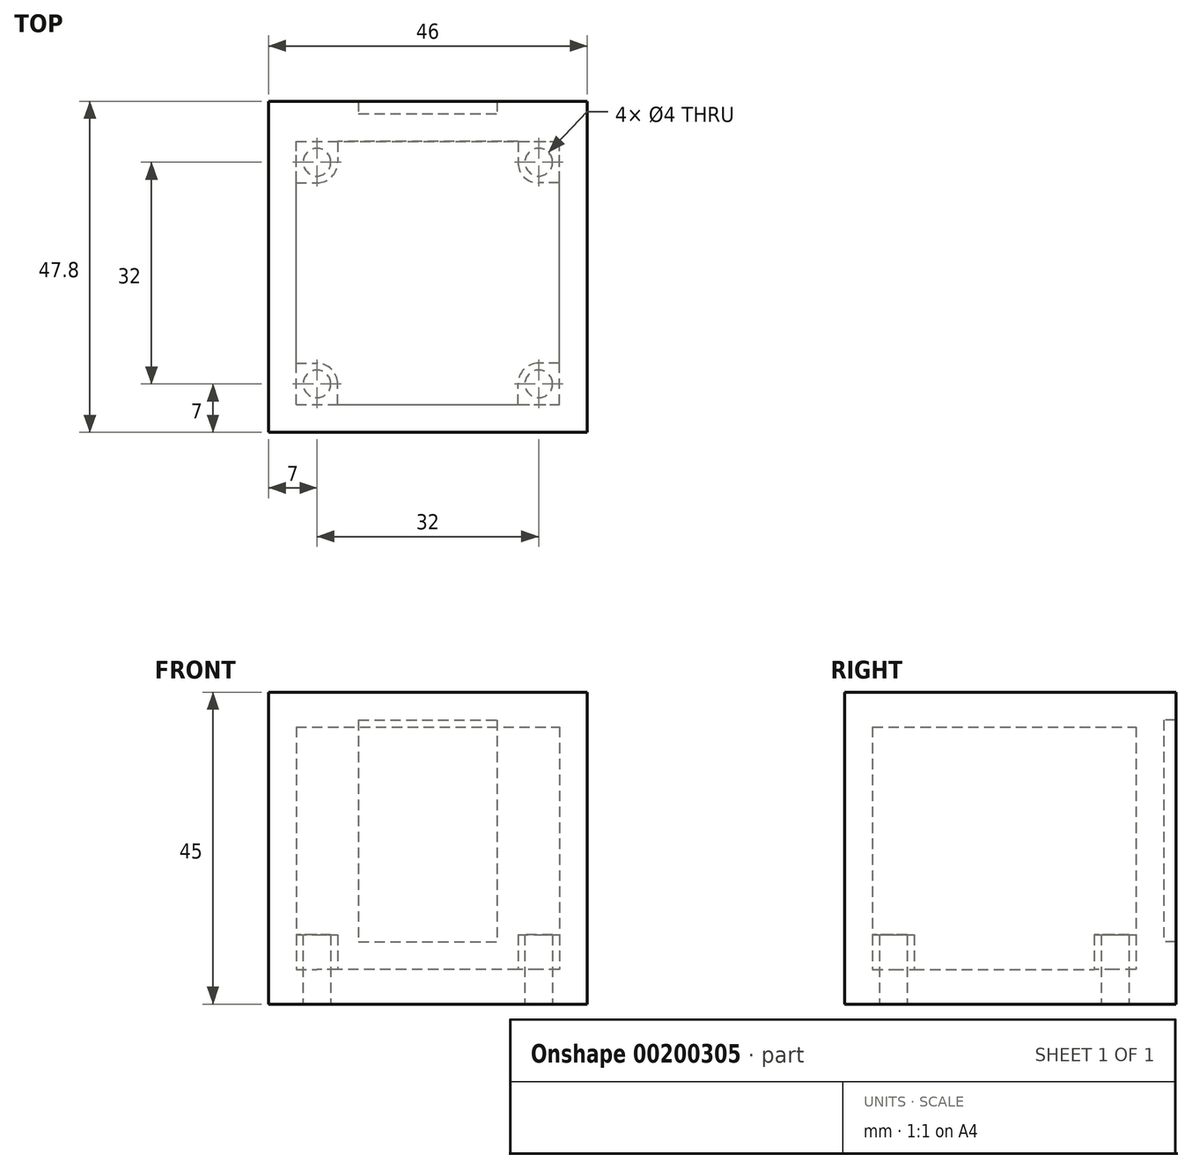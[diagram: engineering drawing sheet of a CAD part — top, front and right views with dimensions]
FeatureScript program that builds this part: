
annotation { "Feature Type Name" : "Feature", "Feature Type Description" : "" }
export const myFeature = defineFeature(function(context is Context, id is Id, definition is map)
    precondition{}
    {
        {
            var Q0;
            Q0=qCreatedBy(makeId("Top.planeOp"),FACE);
            var sketch = newSketch(context, id + "F0", { "sketchPlane" : qUnion([Q0])});
            skLineSegment(sketch, "E0.bottom", {"start": v(0, 0) * mm, "end": v(1000, 0) * mm, "construction": true});
            skLineSegment(sketch, "E0.top", {"start": v(0, 1000) * mm, "end": v(1000, 1000) * mm, "construction": true});
            skLineSegment(sketch, "E0.left", {"start": v(0, 0) * mm, "end": v(0, 1000) * mm, "construction": true});
            skLineSegment(sketch, "E0.right", {"start": v(1000, 0) * mm, "end": v(1000, 1000) * mm, "construction": true});
            skLineSegment(sketch, "E1.bottom", {"start": v(0, 0) * mm, "end": v(100, 0) * mm, "construction": true});
            skLineSegment(sketch, "E1.top", {"start": v(0, 100) * mm, "end": v(100, 100) * mm, "construction": true});
            skLineSegment(sketch, "E1.left", {"start": v(0, 0) * mm, "end": v(0, 100) * mm, "construction": true});
            skLineSegment(sketch, "E1.right", {"start": v(100, 0) * mm, "end": v(100, 100) * mm, "construction": true});
            skPoint(sketch, "E2", {"position": v(100, 100) * mm});
            skSolve(sketch);
        }
        {
            var Q0;
            Q0=qCreatedBy(makeId("Top.planeOp"),FACE);
            var sketch = newSketch(context, id + "F1", { "sketchPlane" : qUnion([Q0])});
            skLineSegment(sketch, "E3.bottom", {"start": v(100, 100) * mm, "end": v(146, 100) * mm});
            skLineSegment(sketch, "E3.top", {"start": v(100, 146) * mm, "end": v(146, 146) * mm});
            skLineSegment(sketch, "E3.left", {"start": v(100, 100) * mm, "end": v(100, 146) * mm});
            skLineSegment(sketch, "E3.right", {"start": v(146, 100) * mm, "end": v(146, 146) * mm});
            skLineSegment(sketch, "E4.0", {"start": v(104, 142) * mm, "end": v(142, 142) * mm});
            skLineSegment(sketch, "E4.1", {"start": v(104, 104) * mm, "end": v(104, 142) * mm});
            skLineSegment(sketch, "E4.2", {"start": v(104, 104) * mm, "end": v(142, 104) * mm});
            skLineSegment(sketch, "E4.3", {"start": v(142, 104) * mm, "end": v(142, 142) * mm});
            skCircle(sketch, "E5", {"center": v(107, 139) * mm, "radius": 2 * mm});
            skCircle(sketch, "E6", {"center": v(139, 139) * mm, "radius": 2 * mm});
            skCircle(sketch, "E7", {"center": v(107, 107) * mm, "radius": 2 * mm});
            skCircle(sketch, "E8", {"center": v(139, 107) * mm, "radius": 2 * mm});
            skLineSegment(sketch, "E9.bottom", {"start": v(139, 139) * mm, "end": v(107, 139) * mm, "construction": true});
            skLineSegment(sketch, "E9.top", {"start": v(139, 107) * mm, "end": v(107, 107) * mm, "construction": true});
            skLineSegment(sketch, "E9.left", {"start": v(139, 139) * mm, "end": v(139, 107) * mm, "construction": true});
            skLineSegment(sketch, "E9.right", {"start": v(107, 139) * mm, "end": v(107, 107) * mm, "construction": true});
            skPoint(sketch, "E9.middle", {"position": v(123, 123) * mm});
            skPoint(sketch, "E9.middle.positionSnap0", {"position": v(104, 123) * mm});
            skPoint(sketch, "E9.middle.positionSnap1", {"position": v(123, 142) * mm});
            skPoint(sketch, "E9.centerSnap0", {"position": v(104, 123) * mm});
            skPoint(sketch, "E9.centerSnap1", {"position": v(123, 142) * mm});
            skLineSegment(sketch, "E10", {"start": v(107, 136) * mm, "end": v(104, 136) * mm});
            skLineSegment(sketch, "E11", {"start": v(110, 139) * mm, "end": v(110, 142) * mm});
            skArc(sketch, "E12", {"start": v(107, 136) * mm, "mid": v(109.12, 136.88) * mm, "end": v(110, 139) * mm});
            skLineSegment(sketch, "E13", {"start": v(139, 136) * mm, "end": v(142, 136) * mm});
            skLineSegment(sketch, "E14", {"start": v(123, 95.95) * mm, "end": v(123, 88.68) * mm, "construction": true});
            skPoint(sketch, "E14.startSnap0", {"position": v(123, 100) * mm});
            skLineSegment(sketch, "E15.MirrorCS", {"start": v(136, 139) * mm, "end": v(136, 142) * mm});
            skArc(sketch, "E16.MirrorCS", {"start": v(139, 136) * mm, "mid": v(136.88, 136.88) * mm, "end": v(136, 139) * mm});
            skLineSegment(sketch, "E17", {"start": v(96.4, 123) * mm, "end": v(88.24, 123) * mm, "construction": true});
            skArc(sketch, "E18.MirrorCS", {"start": v(107, 110) * mm, "mid": v(109.12, 109.12) * mm, "end": v(110, 107) * mm});
            skLineSegment(sketch, "E19.MirrorCS", {"start": v(110, 107) * mm, "end": v(110, 104) * mm});
            skLineSegment(sketch, "E20.MirrorCS", {"start": v(107, 110) * mm, "end": v(104, 110) * mm});
            skLineSegment(sketch, "E21.MirrorCS", {"start": v(139, 110) * mm, "end": v(142, 110) * mm});
            skArc(sketch, "E22.MirrorCS", {"start": v(139, 110) * mm, "mid": v(136.88, 109.12) * mm, "end": v(136, 107) * mm});
            skLineSegment(sketch, "E23.MirrorCS", {"start": v(136, 107) * mm, "end": v(136, 104) * mm});
            skLineSegment(sketch, "E24", {"start": v(104, 142) * mm, "end": v(104, 146) * mm});
            skLineSegment(sketch, "E25", {"start": v(142, 142) * mm, "end": v(142, 146) * mm});
            skSolve(sketch);
        }
        {
            var Q0;
            Q0=makeQuery(id+"F1.imprint","IMPRINT",FACE,{"disambiguationData":[TD([[makeQuery(id+"F1.imprint","IMPRINT",EDGE,{"derivedFrom":sQuery(id+"F1.wireOp",EDGE,"E5")}),-1.0]])]});
            var Q1;
            {var subQ6=sQuery(id+"F1.wireOp",EDGE,"E10");Q1=makeQuery(id+"F1.imprint","IMPRINT",FACE,{"disambiguationData":[TD([[makeQuery(id+"F1.imprint","IMPRINT",EDGE,{"derivedFrom":subQ6}),1.0]])]});}
            var Q2;
            Q2=makeQuery(id+"F1.imprint","IMPRINT",FACE,{"disambiguationData":[TD([[makeQuery(id+"F1.imprint","IMPRINT",EDGE,{"derivedFrom":sQuery(id+"F1.wireOp",EDGE,"E3.bottom")}),1.0]])]});
            var Q3;
            Q3=makeQuery(id+"F1.imprint","IMPRINT",FACE,{"disambiguationData":[TD([[makeQuery(id+"F1.imprint","IMPRINT",EDGE,{"derivedFrom":sQuery(id+"F1.wireOp",EDGE,"E6")}),-1.0]])]});
            var Q4;
            Q4=makeQuery(id+"F1.imprint","IMPRINT",FACE,{"disambiguationData":[TD([[makeQuery(id+"F1.imprint","IMPRINT",EDGE,{"derivedFrom":sQuery(id+"F1.wireOp",EDGE,"E7")}),-1.0]])]});
            var Q5;
            Q5=makeQuery(id+"F1.imprint","IMPRINT",FACE,{"disambiguationData":[TD([[makeQuery(id+"F1.imprint","IMPRINT",EDGE,{"derivedFrom":sQuery(id+"F1.wireOp",EDGE,"E8")}),-1.0]])]});
            var Q6;
            {var subQ3=sQuery(id+"F1.wireOp",EDGE,"E24");Q6=makeQuery(id+"F1.imprint","IMPRINT",FACE,{"disambiguationData":[TD([[makeQuery(id+"F1.imprint","IMPRINT",EDGE,{"derivedFrom":subQ3}),-1.0]])]});}
            extrude(context, id + "F2", {"entities" : qUnion([Q0, Q1, Q2, Q3, Q4, Q5, Q6]), "depth" : 5 * mm});
        }
        {
            var Q0;
            Q0=makeQuery(id+"F1.imprint","IMPRINT",FACE,{"disambiguationData":[TD([[makeQuery(id+"F1.imprint","IMPRINT",EDGE,{"derivedFrom":sQuery(id+"F1.wireOp",EDGE,"E5")}),-1.0]])]});
            var Q1;
            Q1=makeQuery(id+"F1.imprint","IMPRINT",FACE,{"disambiguationData":[TD([[makeQuery(id+"F1.imprint","IMPRINT",EDGE,{"derivedFrom":sQuery(id+"F1.wireOp",EDGE,"E6")}),-1.0]])]});
            var Q2;
            Q2=makeQuery(id+"F1.imprint","IMPRINT",FACE,{"disambiguationData":[TD([[makeQuery(id+"F1.imprint","IMPRINT",EDGE,{"derivedFrom":sQuery(id+"F1.wireOp",EDGE,"E7")}),-1.0]])]});
            var Q3;
            Q3=makeQuery(id+"F1.imprint","IMPRINT",FACE,{"disambiguationData":[TD([[makeQuery(id+"F1.imprint","IMPRINT",EDGE,{"derivedFrom":sQuery(id+"F1.wireOp",EDGE,"E8")}),-1.0]])]});
            extrude(context, id + "F3", {"entities" : qUnion([Q0, Q1, Q2, Q3]), "operationType" : NewBodyOperationType.ADD, "depth" : 10 * mm});
        }
        {
            var Q0;
            {var subQ3=sQuery(id+"F1.wireOp",EDGE,"E24");Q0=makeQuery(id+"F1.imprint","IMPRINT",FACE,{"disambiguationData":[TD([[makeQuery(id+"F1.imprint","IMPRINT",EDGE,{"derivedFrom":subQ3}),-1.0]])]});}
            extrude(context, id + "F4", {"entities" : qUnion([Q0]), "operationType" : NewBodyOperationType.ADD, "depth" : 45 * mm});
        }
        {
            var Q0;
            Q0=makeQuery(id+"F1.imprint","IMPRINT",FACE,{"disambiguationData":[TD([[makeQuery(id+"F1.imprint","IMPRINT",EDGE,{"derivedFrom":sQuery(id+"F1.wireOp",EDGE,"E3.bottom")}),1.0]])]});
            extrude(context, id + "F5", {"entities" : qUnion([Q0]), "depth" : 45 * mm, "hasSecondDirection" : true, "secondDirectionOppositeDirection" : false, "secondDirectionDepth" : 5 * mm});
        }
        {
            var Q0;
            {var subQ7=sQuery(id+"F1.wireOp",EDGE,"E10");Q0=makeQuery(id+"F1.imprint","IMPRINT",FACE,{"disambiguationData":[TD([[makeQuery(id+"F1.imprint","IMPRINT",EDGE,{"derivedFrom":subQ7}),1.0]])]});}
            var Q1;
            Q1=makeQuery(id+"F1.imprint","IMPRINT",FACE,{"disambiguationData":[TD([[makeQuery(id+"F1.imprint","IMPRINT",EDGE,{"derivedFrom":sQuery(id+"F1.wireOp",EDGE,"E7")}),-1.0]])]});
            var Q2;
            Q2=makeQuery(id+"F1.imprint","IMPRINT",FACE,{"disambiguationData":[TD([[makeQuery(id+"F1.imprint","IMPRINT",EDGE,{"derivedFrom":sQuery(id+"F1.wireOp",EDGE,"E7")}),1.0]])]});
            var Q3;
            Q3=makeQuery(id+"F1.imprint","IMPRINT",FACE,{"disambiguationData":[TD([[makeQuery(id+"F1.imprint","IMPRINT",EDGE,{"derivedFrom":sQuery(id+"F1.wireOp",EDGE,"E8")}),1.0]])]});
            var Q4;
            Q4=makeQuery(id+"F1.imprint","IMPRINT",FACE,{"disambiguationData":[TD([[makeQuery(id+"F1.imprint","IMPRINT",EDGE,{"derivedFrom":sQuery(id+"F1.wireOp",EDGE,"E8")}),-1.0]])]});
            var Q5;
            Q5=makeQuery(id+"F1.imprint","IMPRINT",FACE,{"disambiguationData":[TD([[makeQuery(id+"F1.imprint","IMPRINT",EDGE,{"derivedFrom":sQuery(id+"F1.wireOp",EDGE,"E6")}),-1.0]])]});
            var Q6;
            Q6=makeQuery(id+"F1.imprint","IMPRINT",FACE,{"disambiguationData":[TD([[makeQuery(id+"F1.imprint","IMPRINT",EDGE,{"derivedFrom":sQuery(id+"F1.wireOp",EDGE,"E5")}),-1.0]])]});
            var Q7;
            Q7=makeQuery(id+"F1.imprint","IMPRINT",FACE,{"disambiguationData":[TD([[makeQuery(id+"F1.imprint","IMPRINT",EDGE,{"derivedFrom":sQuery(id+"F1.wireOp",EDGE,"E5")}),1.0]])]});
            var Q8;
            Q8=makeQuery(id+"F1.imprint","IMPRINT",FACE,{"disambiguationData":[TD([[makeQuery(id+"F1.imprint","IMPRINT",EDGE,{"derivedFrom":sQuery(id+"F1.wireOp",EDGE,"E6")}),1.0]])]});
            extrude(context, id + "F6", {"entities" : qUnion([Q0, Q1, Q2, Q3, Q4, Q5, Q6, Q7, Q8]), "operationType" : NewBodyOperationType.ADD, "depth" : 45 * mm, "hasSecondDirection" : true, "secondDirectionOppositeDirection" : false, "secondDirectionDepth" : 40 * mm});
        }
        {
            var Q0;
            {var subQ0=sQuery(id+"F1.wireOp",EDGE,"E3.top");Q0=makeQuery(id+"F4.boolean.opBoolean","MERGE",FACE,{"derivedFrom":[makeQuery(id+"F2.opExtrude","SWEPT_FACE",FACE,{"disambiguationData":[OSD([subQ0])]}),makeQuery(id+"F4.opExtrude","SWEPT_FACE",FACE,{"disambiguationData":[OSD([subQ0])]})]});}
            var sketch = newSketch(context, id + "F7", { "sketchPlane" : qUnion([Q0])});
            skLineSegment(sketch, "E26.bottom", {"start": v(-113, 41) * mm, "end": v(-133, 41) * mm});
            skLineSegment(sketch, "E26.top", {"start": v(-113, 9) * mm, "end": v(-133, 9) * mm});
            skLineSegment(sketch, "E26.left", {"start": v(-113, 41) * mm, "end": v(-113, 9) * mm});
            skLineSegment(sketch, "E26.right", {"start": v(-133, 41) * mm, "end": v(-133, 9) * mm});
            skPoint(sketch, "E26.middle", {"position": v(-123, 25) * mm});
            skPoint(sketch, "E26.middle.positionSnap0", {"position": v(-142, 25) * mm});
            skPoint(sketch, "E26.middle.positionSnap1", {"position": v(-123, 45) * mm});
            skPoint(sketch, "E26.centerSnap0", {"position": v(-142, 25) * mm});
            skPoint(sketch, "E26.centerSnap1", {"position": v(-123, 45) * mm});
            skSolve(sketch);
        }
        {
            var Q0;
            Q0=makeQuery(id+"F7.imprint","IMPRINT",FACE,{"disambiguationData":[TD([[makeQuery(id+"F7.imprint","IMPRINT",EDGE,{"derivedFrom":sQuery(id+"F7.wireOp",EDGE,"E26.bottom")}),-1.0]])]});
            extrude(context, id + "F8", {"entities" : qUnion([Q0]), "operationType" : NewBodyOperationType.ADD, "depth" : 1.8 * mm});
        }
    });
